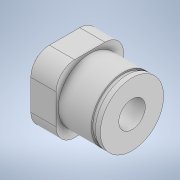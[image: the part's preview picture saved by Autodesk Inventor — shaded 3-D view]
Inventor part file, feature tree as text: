
AUTODESK INVENTOR PART (.ipt)
format: ipt  version: 2020 (Build 240168000, 168)  size: 174,592 bytes
history: native  units: mm
features: extrude x6, sketch x6, fillet x2
ambient origin geometry x8: Origin, YZ Plane, XZ Plane, XY Plane, X Axis, Y Axis, Z Axis, Center Point
bodies: Solid1 (feature_tree)
feature tree (14):
  extrude  "Extrusion1"  Depth=20.32mm
  extrude  "Extrusion2"  Depth=12.7mm
  fillet  "Fillet1"  Radius=12.7mm
  extrude  "Extrusion3"  Depth=5.588mm
  extrude  "Extrusion4"  Depth=1.5mm TaperAngle=0.0deg
  extrude  "Extrusion5"  Depth=25.0mm TaperAngle=0.0deg
  extrude  "Extrusion6"  Depth=5.0mm TaperAngle=0.0deg
  fillet  "Fillet2"  Radius=2.0mm
  sketch  "Sketch1"  dims[d0=20.32mm d1=20.32mm]
  sketch  "Sketch2"  dims[d2=7.62mm d3=0.0mm d4=19.05mm d5=12.7mm d6=0.0mm]
  sketch  "Sketch3"  dims[d7=5.588mm d8=18.25mm]
  sketch  "Sketch4"  dims[d9=2.72mm d10=0.0mm d11=1.5mm d12=0.0mm]
  sketch  "Sketch5"  dims[d13=8.0mm d14=25.0mm d15=0.0mm]
  sketch  "Sketch6"  dims[d16=10.0mm d17=5.0mm d18=0.0mm d19=2.0mm]
